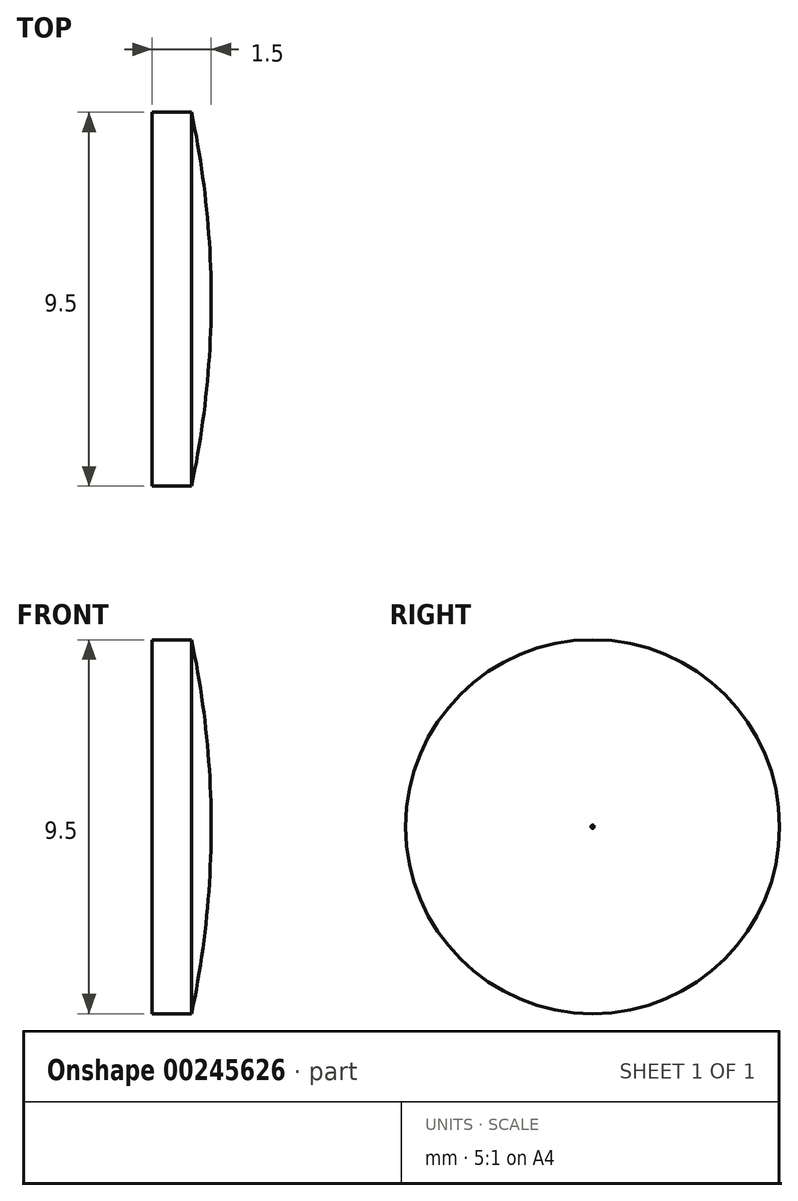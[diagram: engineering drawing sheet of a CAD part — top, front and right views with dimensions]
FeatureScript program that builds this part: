
annotation { "Feature Type Name" : "Feature", "Feature Type Description" : "" }
export const myFeature = defineFeature(function(context is Context, id is Id, definition is map)
    precondition{}
    {
        {
            var Q0;
            Q0=qCreatedBy(makeId("Front.planeOp"),FACE);
            var sketch = newSketch(context, id + "F0", { "sketchPlane" : qUnion([Q0])});
            skLineSegment(sketch, "E0", {"start": v(0, 0) * mm, "end": v(1.5, 0) * mm});
            skLineSegment(sketch, "E1", {"start": v(0, 0) * mm, "end": v(0, 4.75) * mm});
            skLineSegment(sketch, "E2", {"start": v(0, 4.75) * mm, "end": v(1, 4.75) * mm});
            skArc(sketch, "E3", {"start": v(1.5, 0) * mm, "mid": v(1.37, 2.39) * mm, "end": v(1, 4.75) * mm});
            skSolve(sketch);
        }
        {
            var Q0;
            Q0=makeQuery(id+"F0.imprint","IMPRINT",FACE,{"disambiguationData":[TD([[makeQuery(id+"F0.imprint","IMPRINT",EDGE,{"derivedFrom":sQuery(id+"F0.wireOp",EDGE,"E0")}),1.0]])]});
            var Q1;
            Q1=sQuery(id+"F0.wireOp",EDGE,"E0");
            revolve(context, id + "F1", {"entities" : qUnion([Q0]), "axis" : qUnion([Q1]), "revolveType" : RevolveType.FULL});
        }
    });
